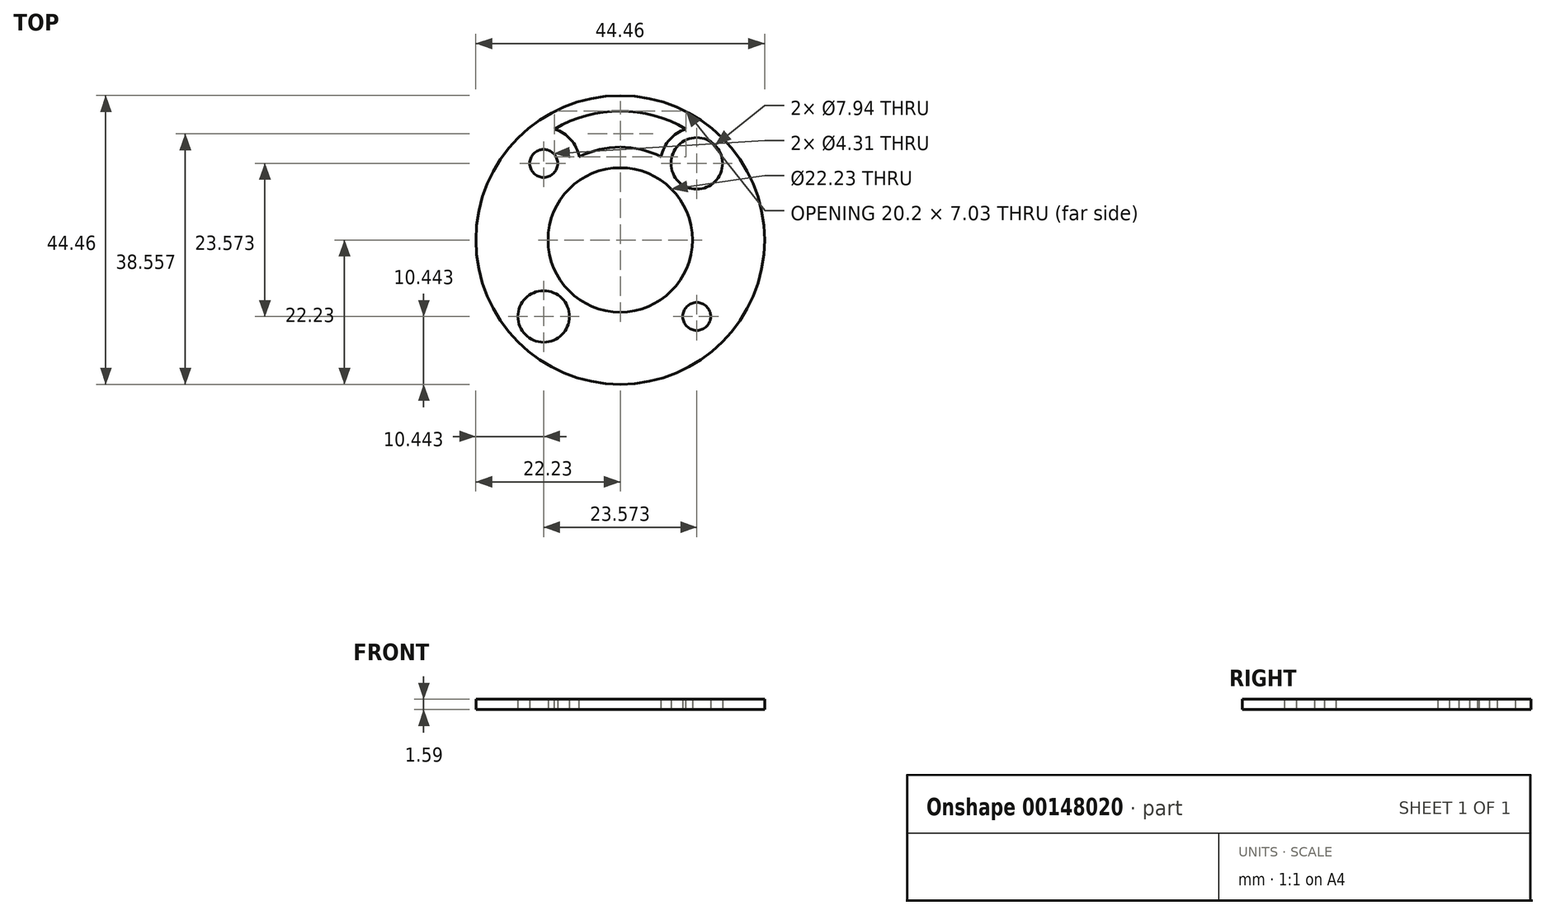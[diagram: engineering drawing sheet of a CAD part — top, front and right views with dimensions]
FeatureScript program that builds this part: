
annotation { "Feature Type Name" : "Feature", "Feature Type Description" : "" }
export const myFeature = defineFeature(function(context is Context, id is Id, definition is map)
    precondition{}
    {
        {
            var Q0;
            Q0=qCreatedBy(makeId("Top.planeOp"),FACE);
            var sketch = newSketch(context, id + "F0", { "sketchPlane" : qUnion([Q0])});
            skCircle(sketch, "E0", {"center": v(0, 0) * mm, "radius": 22.23 * mm});
            skCircle(sketch, "E1", {"center": v(0, 0) * mm, "radius": 11.11 * mm});
            skLineSegment(sketch, "E2.bottom", {"start": v(-11.79, 11.79) * mm, "end": v(11.79, 11.79) * mm, "construction": true});
            skLineSegment(sketch, "E2.top", {"start": v(-11.79, -11.79) * mm, "end": v(11.79, -11.79) * mm, "construction": true});
            skLineSegment(sketch, "E2.left", {"start": v(-11.79, 11.79) * mm, "end": v(-11.79, -11.79) * mm, "construction": true});
            skLineSegment(sketch, "E2.right", {"start": v(11.79, 11.79) * mm, "end": v(11.79, -11.79) * mm, "construction": true});
            skCircle(sketch, "E3", {"center": v(11.79, 11.79) * mm, "radius": 3.97 * mm});
            skCircle(sketch, "E4", {"center": v(-11.79, 11.79) * mm, "radius": 2.15 * mm});
            skCircle(sketch, "E5", {"center": v(-11.79, -11.79) * mm, "radius": 3.97 * mm});
            skCircle(sketch, "E6", {"center": v(11.79, -11.79) * mm, "radius": 2.15 * mm});
            skCircle(sketch, "E7", {"center": v(11.79, 11.79) * mm, "radius": 5.56 * mm, "construction": true});
            skSolve(sketch);
        }
        {
            var Q0;
            Q0=qSketchRegion(id+"F0",true);
            extrude(context, id + "F1", {"entities" : qUnion([Q0]), "depth" : 1.59 * mm});
        }
        {
            var Q0;
            Q0=makeQuery(id+"F1.opExtrude","CAP_FACE",FACE,{"disambiguationData":[OSD([sQuery(id+"F0.wireOp",EDGE,"E0"),sQuery(id+"F0.wireOp",EDGE,"E1"),sQuery(id+"F0.wireOp",EDGE,"E3"),sQuery(id+"F0.wireOp",EDGE,"E4"),sQuery(id+"F0.wireOp",EDGE,"E5"),sQuery(id+"F0.wireOp",EDGE,"E6")])],"isStart":false});
            var sketch = newSketch(context, id + "F2", { "sketchPlane" : qUnion([Q0])});
            skArc(sketch, "E8", {"start": v(-6.33, 12.81) * mm, "mid": v(-7.62, 15.47) * mm, "end": v(-10.1, 17.08) * mm});
            skArc(sketch, "E9", {"start": v(10.1, 17.08) * mm, "mid": v(7.62, 15.47) * mm, "end": v(6.33, 12.81) * mm});
            skArc(sketch, "E10", {"start": v(10.1, 17.08) * mm, "mid": v(0, 19.84) * mm, "end": v(-10.1, 17.08) * mm});
            skArc(sketch, "E11", {"start": v(6.33, 12.81) * mm, "mid": v(0, 14.29) * mm, "end": v(-6.33, 12.81) * mm});
            skSolve(sketch);
        }
        {
            var Q0;
            Q0=makeQuery(id+"F2.imprint","IMPRINT",FACE,{"disambiguationData":[TD([[makeQuery(id+"F2.imprint","IMPRINT",EDGE,{"derivedFrom":sQuery(id+"F2.wireOp",EDGE,"E8")}),-1.0]])]});
            var Q1;
            Q1=makeQuery(id+"F1.opExtrude","CAP_FACE",FACE,{"disambiguationData":[OSD([sQuery(id+"F0.wireOp",EDGE,"E0"),sQuery(id+"F0.wireOp",EDGE,"E1"),sQuery(id+"F0.wireOp",EDGE,"E3"),sQuery(id+"F0.wireOp",EDGE,"E4"),sQuery(id+"F0.wireOp",EDGE,"E5"),sQuery(id+"F0.wireOp",EDGE,"E6")])],"isStart":true});
            extrude(context, id + "F3", {"entities" : qUnion([Q0]), "operationType" : NewBodyOperationType.REMOVE, "endBound" : BoundingType.UP_TO_SURFACE, "oppositeDirection" : true, "endBoundEntityFace" : qUnion([Q1]), "depth" : 25.4 * mm});
        }
    });
